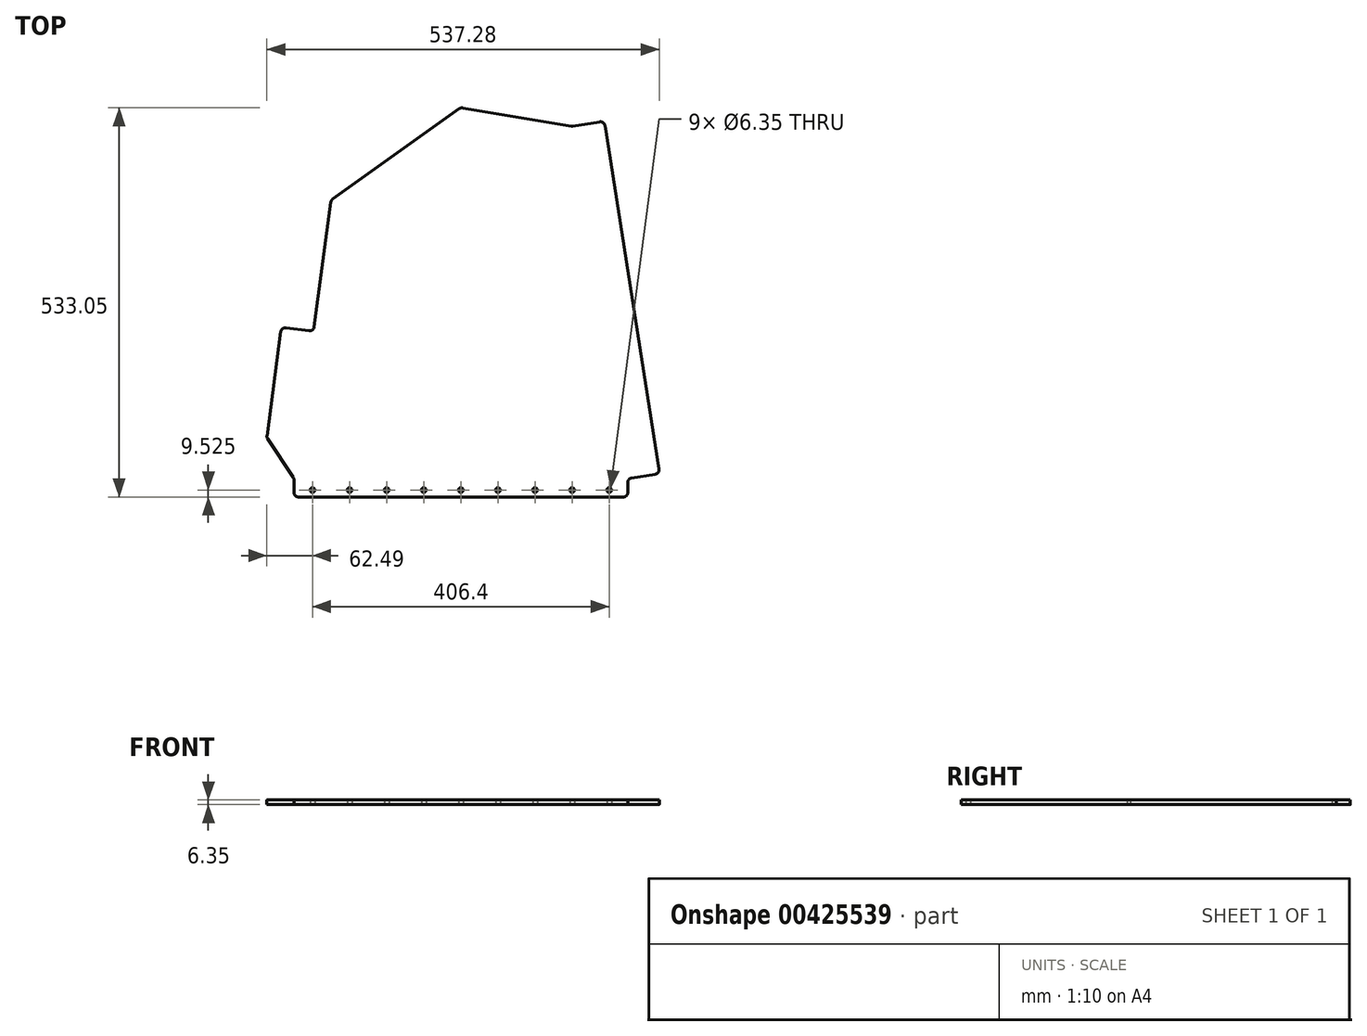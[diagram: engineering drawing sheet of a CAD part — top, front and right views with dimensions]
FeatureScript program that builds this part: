
annotation { "Feature Type Name" : "Feature", "Feature Type Description" : "" }
export const myFeature = defineFeature(function(context is Context, id is Id, definition is map)
    precondition{}
    {
        {
            var Q0;
            Q0=qCreatedBy(makeId("Top.planeOp"),FACE);
            var sketch = newSketch(context, id + "F0", { "sketchPlane" : qUnion([Q0])});
            skLineSegment(sketch, "E0", {"start": v(6.35, 0) * mm, "end": v(450.85, 0) * mm});
            skLineSegment(sketch, "E1", {"start": v(457.2, 0) * mm, "end": v(457.2, 25.4) * mm, "construction": true});
            skLineSegment(sketch, "E2", {"start": v(457.2, 6.35) * mm, "end": v(457.2, 19.97) * mm});
            skLineSegment(sketch, "E3", {"start": v(231.2, 532.97) * mm, "end": v(379.98, 508.17) * mm});
            skLineSegment(sketch, "E4", {"start": v(226.46, 531.87) * mm, "end": v(53.04, 408) * mm});
            skLineSegment(sketch, "E5", {"start": v(50.44, 403.67) * mm, "end": v(27.7, 233.11) * mm});
            skLineSegment(sketch, "E6", {"start": v(26.86, 226.82) * mm, "end": v(-17.2, 232.7) * mm, "construction": true});
            skLineSegment(sketch, "E7", {"start": v(20.56, 227.66) * mm, "end": v(-10.91, 231.85) * mm});
            skLineSegment(sketch, "E8", {"start": v(-18.04, 226.4) * mm, "end": v(-37.03, 84) * mm});
            skLineSegment(sketch, "E9", {"start": v(-36.03, 79.64) * mm, "end": v(-1.06, 27) * mm});
            skLineSegment(sketch, "E10", {"start": v(457.2, 0) * mm, "end": v(457.2, 9.53) * mm, "construction": true});
            skLineSegment(sketch, "E11", {"start": v(488.34, 9.53) * mm, "end": v(-43.14, 9.53) * mm, "construction": true});
            skLineSegment(sketch, "E12", {"start": v(457.2, 9.53) * mm, "end": v(431.8, 9.53) * mm, "construction": true});
            skLineSegment(sketch, "E13", {"start": v(431.8, 9.53) * mm, "end": v(381, 9.53) * mm, "construction": true});
            skLineSegment(sketch, "E14", {"start": v(381, 9.53) * mm, "end": v(330.2, 9.53) * mm, "construction": true});
            skCircle(sketch, "E15", {"center": v(431.8, 9.53) * mm, "radius": 3.17 * mm});
            skLineSegment(sketch, "E16", {"start": v(457.2, 25.4) * mm, "end": v(501.1, 32.33) * mm, "construction": true});
            skLineSegment(sketch, "E17", {"start": v(501.1, 32.33) * mm, "end": v(424.9, 514.93) * mm, "construction": true});
            skLineSegment(sketch, "E18", {"start": v(462.56, 26.25) * mm, "end": v(494.83, 31.34) * mm});
            skLineSegment(sketch, "E19", {"start": v(425.9, 508.66) * mm, "end": v(500.12, 38.6) * mm});
            skLineSegment(sketch, "E20", {"start": v(418.63, 513.94) * mm, "end": v(382.02, 508.16) * mm});
            skCircle(sketch, "E21.1.0.0", {"center": v(381, 9.53) * mm, "radius": 3.17 * mm});
            skCircle(sketch, "E21.2.0.0", {"center": v(330.2, 9.53) * mm, "radius": 3.17 * mm});
            skCircle(sketch, "E21.3.0.0", {"center": v(279.4, 9.53) * mm, "radius": 3.17 * mm});
            skCircle(sketch, "E21.4.0.0", {"center": v(228.6, 9.53) * mm, "radius": 3.17 * mm});
            skCircle(sketch, "E21.5.0.0", {"center": v(177.8, 9.53) * mm, "radius": 3.17 * mm});
            skCircle(sketch, "E21.6.0.0", {"center": v(127, 9.53) * mm, "radius": 3.17 * mm});
            skCircle(sketch, "E21.7.0.0", {"center": v(76.2, 9.53) * mm, "radius": 3.17 * mm});
            skCircle(sketch, "E21.8.0.0", {"center": v(25.4, 9.53) * mm, "radius": 3.17 * mm});
            skLineSegment(sketch, "E22", {"start": v(0, 6.35) * mm, "end": v(0, 23.48) * mm});
            skLineSegment(sketch, "E23", {"start": v(381, 508) * mm, "end": v(393.54, 509.98) * mm, "construction": true});
            skLineSegment(sketch, "E24", {"start": v(371.83, 647.48) * mm, "end": v(499.27, -159.61) * mm, "construction": true});
            skPoint(sketch, "E25.visualSharp", {"position": v(0, 0) * mm});
            skArc(sketch, "E25.filletArc", {"start": v(0, 6.35) * mm, "mid": v(1.86, 1.86) * mm, "end": v(6.35, 0) * mm});
            skPoint(sketch, "E26.visualSharp", {"position": v(0, 25.4) * mm});
            skArc(sketch, "E26.filletArc", {"start": v(0, 23.48) * mm, "mid": v(-0.27, 25.32) * mm, "end": v(-1.06, 27) * mm});
            skPoint(sketch, "E27.visualSharp", {"position": v(-37.35, 81.63) * mm});
            skArc(sketch, "E27.filletArc", {"start": v(-37.03, 84) * mm, "mid": v(-36.92, 81.73) * mm, "end": v(-36.03, 79.64) * mm});
            skPoint(sketch, "E28.visualSharp", {"position": v(-17.2, 232.7) * mm});
            skArc(sketch, "E28.filletArc", {"start": v(-10.91, 231.85) * mm, "mid": v(-15.6, 230.6) * mm, "end": v(-18.04, 226.4) * mm});
            skPoint(sketch, "E29.visualSharp", {"position": v(26.86, 226.82) * mm});
            skArc(sketch, "E29.filletArc", {"start": v(20.56, 227.66) * mm, "mid": v(25.26, 228.9) * mm, "end": v(27.7, 233.11) * mm});
            skPoint(sketch, "E30.visualSharp", {"position": v(50.8, 406.4) * mm});
            skArc(sketch, "E30.filletArc", {"start": v(53.04, 408) * mm, "mid": v(51.29, 406.1) * mm, "end": v(50.44, 403.67) * mm});
            skPoint(sketch, "E31.visualSharp", {"position": v(228.6, 533.4) * mm});
            skArc(sketch, "E31.filletArc", {"start": v(231.2, 532.97) * mm, "mid": v(228.72, 532.9) * mm, "end": v(226.46, 531.87) * mm});
            skPoint(sketch, "E32.visualSharp", {"position": v(381, 508) * mm});
            skArc(sketch, "E32.filletArc", {"start": v(379.98, 508.17) * mm, "mid": v(381, 508.08) * mm, "end": v(382.02, 508.16) * mm});
            skPoint(sketch, "E33.visualSharp", {"position": v(424.9, 514.93) * mm});
            skArc(sketch, "E33.filletArc", {"start": v(425.9, 508.66) * mm, "mid": v(423.36, 512.8) * mm, "end": v(418.63, 513.94) * mm});
            skPoint(sketch, "E34.visualSharp", {"position": v(501.1, 32.33) * mm});
            skArc(sketch, "E34.filletArc", {"start": v(494.83, 31.34) * mm, "mid": v(498.98, 33.88) * mm, "end": v(500.12, 38.6) * mm});
            skPoint(sketch, "E35.visualSharp", {"position": v(457.2, 25.4) * mm});
            skArc(sketch, "E35.filletArc", {"start": v(462.56, 26.25) * mm, "mid": v(458.72, 24.1) * mm, "end": v(457.2, 19.97) * mm});
            skPoint(sketch, "E36.visualSharp", {"position": v(457.2, 0) * mm});
            skArc(sketch, "E36.filletArc", {"start": v(450.85, 0) * mm, "mid": v(455.34, 1.86) * mm, "end": v(457.2, 6.35) * mm});
            skLineSegment(sketch, "E37", {"start": v(26.86, 226.82) * mm, "end": v(20.56, 227.66) * mm, "construction": true});
            skLineSegment(sketch, "E38", {"start": v(49.71, 494.32) * mm, "end": v(-18.8, -19.56) * mm, "construction": true});
            skSolve(sketch);
        }
        {
            var Q0;
            Q0 = qSketchRegion(id + "F0", true);
            extrude(context, id + "F1", {"entities" : qUnion([Q0]), "depth" : 6.35 * mm});
        }
    });
